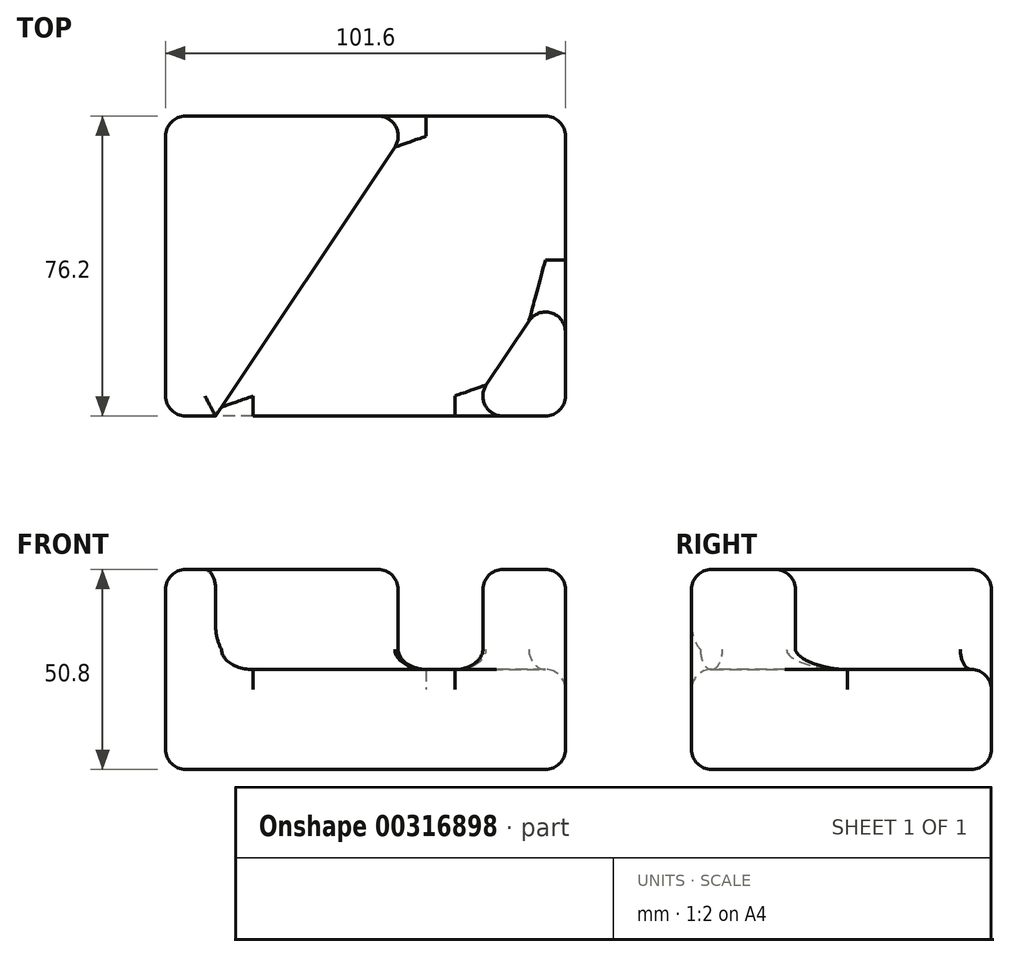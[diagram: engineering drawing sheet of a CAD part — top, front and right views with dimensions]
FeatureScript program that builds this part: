
annotation { "Feature Type Name" : "Feature", "Feature Type Description" : "" }
export const myFeature = defineFeature(function(context is Context, id is Id, definition is map)
    precondition{}
    {
        {
            var Q0;
            Q0=qCreatedBy(makeId("Top.planeOp"),FACE);
            var sketch = newSketch(context, id + "F0", { "sketchPlane" : qUnion([Q0])});
            skLineSegment(sketch, "E0", {"start": v(-66.72, 42.28) * mm, "end": v(-66.72, -33.92) * mm});
            skLineSegment(sketch, "E1", {"start": v(-66.72, -33.92) * mm, "end": v(34.88, -33.92) * mm});
            skLineSegment(sketch, "E2", {"start": v(34.88, -33.92) * mm, "end": v(34.88, 42.28) * mm});
            skLineSegment(sketch, "E3", {"start": v(34.88, 42.28) * mm, "end": v(-66.72, 42.28) * mm});
            skSolve(sketch);
        }
        {
            var Q0;
            Q0=makeQuery(id+"F0.imprint","IMPRINT",FACE,{"disambiguationData":[TD([[makeQuery(id+"F0.imprint","IMPRINT",EDGE,{"derivedFrom":sQuery(id+"F0.wireOp",EDGE,"E0")}),1.0]])]});
            extrude(context, id + "F1", {"entities" : qUnion([Q0]), "depth" : 50.8 * mm});
        }
        {
            var Q0;
            Q0=makeQuery(id+"F1.opExtrude","CAP_FACE",FACE,{"disambiguationData":[OSD([sQuery(id+"F0.wireOp",EDGE,"E0"),sQuery(id+"F0.wireOp",EDGE,"E1"),sQuery(id+"F0.wireOp",EDGE,"E2"),sQuery(id+"F0.wireOp",EDGE,"E3")])],"isStart":false});
            var sketch = newSketch(context, id + "F2", { "sketchPlane" : qUnion([Q0])});
            skLineSegment(sketch, "E4", {"start": v(9.48, -33.92) * mm, "end": v(34.88, 4.18) * mm});
            skLineSegment(sketch, "E5", {"start": v(9.48, -33.92) * mm, "end": v(34.88, -33.92) * mm});
            skLineSegment(sketch, "E6", {"start": v(34.88, -33.92) * mm, "end": v(34.88, 4.18) * mm});
            skPoint(sketch, "E7.start.orphan", {"position": v(0, 42.28) * mm});
            skLineSegment(sketch, "E8", {"start": v(9.48, -33.92) * mm, "end": v(-54.02, -33.92) * mm});
            skLineSegment(sketch, "E9", {"start": v(34.88, 42.28) * mm, "end": v(-3.22, 42.28) * mm});
            skLineSegment(sketch, "E10", {"start": v(-3.22, 42.28) * mm, "end": v(-54.02, -33.92) * mm});
            skSolve(sketch);
        }
        {
            var Q0;
            {var subQ1=sQuery(id+"F2.wireOp",EDGE,"E4");Q0=makeQuery(id+"F2.imprint","IMPRINT",FACE,{"disambiguationData":[TD([[makeQuery(id+"F2.imprint","IMPRINT",EDGE,{"derivedFrom":subQ1}),1.0]])]});}
            extrude(context, id + "F3", {"entities" : qUnion([Q0]), "operationType" : NewBodyOperationType.REMOVE, "oppositeDirection" : true, "depth" : 25.4 * mm});
        }
        {
            var Q0;
            {var subQ0=sQuery(id+"F0.wireOp",EDGE,"E0");var subQ1=sQuery(id+"F0.wireOp",EDGE,"E3");var subQ2=sQuery(id+"F0.wireOp",EDGE,"E1");Q0=makeQuery(id+"F3.boolean.opBoolean","SPLIT",FACE,{"disambiguationData":[TD([makeQuery(id+"F1.opExtrude","SWEPT_FACE",FACE,{"disambiguationData":[OSD([subQ0])]})])],"derivedFrom":makeQuery(id+"F1.opExtrude","CAP_FACE",FACE,{"disambiguationData":[OSD([subQ0,subQ2,sQuery(id+"F0.wireOp",EDGE,"E2"),subQ1])],"isStart":false})});}
            var Q1;
            Q1=makeQuery(id+"F1.opExtrude","SWEPT_FACE",FACE,{"disambiguationData":[OSD([sQuery(id+"F0.wireOp",EDGE,"E3")])]});
            var Q2;
            Q2=makeQuery(id+"F1.opExtrude","SWEPT_FACE",FACE,{"disambiguationData":[OSD([sQuery(id+"F0.wireOp",EDGE,"E0")])]});
            var Q3;
            Q3=makeQuery(id+"F3.boolean.opBoolean","COPY",FACE,{"derivedFrom":makeQuery(id+"F3.opExtrude","CAP_FACE",FACE,{"disambiguationData":[OSD([sQuery(id+"F0.wireOp",EDGE,"E2"),sQuery(id+"F2.wireOp",EDGE,"E4"),sQuery(id+"F2.wireOp",EDGE,"E8"),sQuery(id+"F2.wireOp",EDGE,"E9"),sQuery(id+"F2.wireOp",EDGE,"E10")])],"isStart":false})});
            var Q4;
            Q4=makeQuery(id+"F3.boolean.opBoolean","COPY",FACE,{"derivedFrom":makeQuery(id+"F3.opExtrude","SWEPT_FACE",FACE,{"disambiguationData":[OSD([sQuery(id+"F2.wireOp",EDGE,"E4")])]})});
            var Q5;
            Q5=makeQuery(id+"F1.opExtrude","CAP_FACE",FACE,{"disambiguationData":[OSD([sQuery(id+"F0.wireOp",EDGE,"E0"),sQuery(id+"F0.wireOp",EDGE,"E1"),sQuery(id+"F0.wireOp",EDGE,"E2"),sQuery(id+"F0.wireOp",EDGE,"E3")])],"isStart":true});
            var Q6;
            Q6=makeQuery(id+"F1.opExtrude","SWEPT_FACE",FACE,{"disambiguationData":[OSD([sQuery(id+"F0.wireOp",EDGE,"E2")])]});
            var Q7;
            {var subQ0=sQuery(id+"F0.wireOp",EDGE,"E2");var subQ1=sQuery(id+"F0.wireOp",EDGE,"E1");Q7=makeQuery(id+"F3.boolean.opBoolean","SPLIT",EDGE,{"disambiguationData":[TD([makeQuery(id+"F1.opExtrude","SWEPT_FACE",FACE,{"disambiguationData":[OSD([subQ0])]})])],"derivedFrom":makeQuery(id+"F1.opExtrude","CAP_EDGE",EDGE,{"disambiguationData":[OSD([subQ1])],"isStart":false})});}
            fillet(context, id + "F4", {"entities" : qUnion([Q0, Q1, Q2, Q3, Q4, Q5, Q6, Q7]), "radius" : 5.08 * mm, "tangentPropagation" : true, "allowEdgeOverflow" : false});
        }
    });
